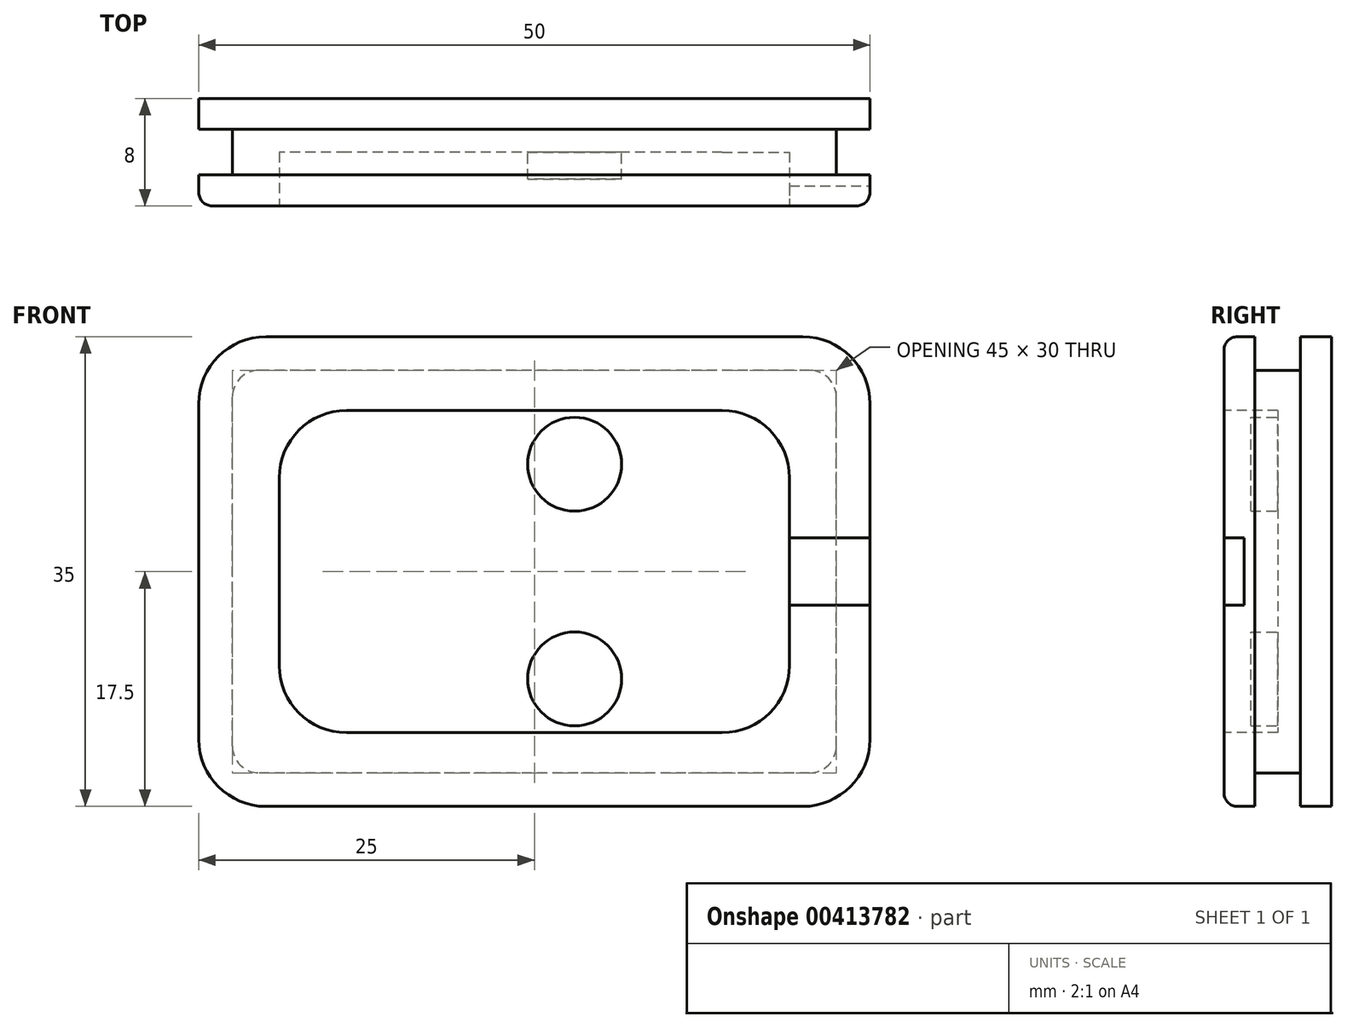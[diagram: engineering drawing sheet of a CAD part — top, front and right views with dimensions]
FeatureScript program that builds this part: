
annotation { "Feature Type Name" : "Feature", "Feature Type Description" : "" }
export const myFeature = defineFeature(function(context is Context, id is Id, definition is map)
    precondition{}
    {
        {
            var Q0;
            Q0=qCreatedBy(makeId("Front.planeOp"),FACE);
            var sketch = newSketch(context, id + "F0", { "sketchPlane" : qUnion([Q0])});
            skLineSegment(sketch, "E0", {"start": v(0, 0) * mm, "end": v(50, 0) * mm});
            skLineSegment(sketch, "E1", {"start": v(50, 0) * mm, "end": v(50, 35) * mm});
            skLineSegment(sketch, "E2", {"start": v(50, 35) * mm, "end": v(0, 35) * mm});
            skLineSegment(sketch, "E3", {"start": v(0, 35) * mm, "end": v(0, 0) * mm});
            skSolve(sketch);
        }
        {
            var Q0;
            Q0=makeQuery(id+"F0.imprint","IMPRINT",FACE,{"disambiguationData":[TD([[makeQuery(id+"F0.imprint","IMPRINT",EDGE,{"derivedFrom":sQuery(id+"F0.wireOp",EDGE,"E0")}),1.0]])]});
            extrude(context, id + "F1", {"entities" : qUnion([Q0]), "depth" : 8 * mm});
        }
        {
            var Q0;
            Q0=makeQuery(id+"F1.opExtrude","CAP_FACE",FACE,{"disambiguationData":[OSD([sQuery(id+"F0.wireOp",EDGE,"E0"),sQuery(id+"F0.wireOp",EDGE,"E1"),sQuery(id+"F0.wireOp",EDGE,"E2"),sQuery(id+"F0.wireOp",EDGE,"E3")])],"isStart":false});
            var sketch = newSketch(context, id + "F2", { "sketchPlane" : qUnion([Q0])});
            skLineSegment(sketch, "E4", {"start": v(6, 5.5) * mm, "end": v(44, 5.5) * mm});
            skLineSegment(sketch, "E5", {"start": v(44, 29.5) * mm, "end": v(6, 29.5) * mm});
            skLineSegment(sketch, "E6", {"start": v(6, 29.5) * mm, "end": v(6, 5.5) * mm});
            skLineSegment(sketch, "E7", {"start": v(44, 29.5) * mm, "end": v(44, 5.5) * mm});
            skSolve(sketch);
        }
        {
            var Q0;
            Q0=makeQuery(id+"F2.imprint","IMPRINT",FACE,{"disambiguationData":[TD([[makeQuery(id+"F2.imprint","IMPRINT",EDGE,{"derivedFrom":sQuery(id+"F2.wireOp",EDGE,"E4")}),1.0]])]});
            extrude(context, id + "F3", {"entities" : qUnion([Q0]), "operationType" : NewBodyOperationType.REMOVE, "oppositeDirection" : true, "depth" : 4 * mm});
        }
        {
            var Q0;
            Q0=makeQuery(id+"F3.boolean.opBoolean","COPY",FACE,{"derivedFrom":makeQuery(id+"F3.opExtrude","CAP_FACE",FACE,{"disambiguationData":[OSD([sQuery(id+"F2.wireOp",EDGE,"E4"),sQuery(id+"F2.wireOp",EDGE,"E5"),sQuery(id+"F2.wireOp",EDGE,"E6"),sQuery(id+"F2.wireOp",EDGE,"E7")])],"isStart":false})});
            var sketch = newSketch(context, id + "F4", { "sketchPlane" : qUnion([Q0])});
            skCircle(sketch, "E8", {"center": v(28, 9.5) * mm, "radius": 3.5 * mm});
            skSolve(sketch);
        }
        {
            var Q0;
            Q0=makeQuery(id+"F4.imprint","IMPRINT",FACE,{"disambiguationData":[TD([[makeQuery(id+"F4.imprint","IMPRINT",EDGE,{"derivedFrom":sQuery(id+"F4.wireOp",EDGE,"E8")}),-1.0]])]});
            var sketch = newSketch(context, id + "F5", { "sketchPlane" : qUnion([Q0])});
            skCircle(sketch, "E9", {"center": v(28, 25.5) * mm, "radius": 3.5 * mm});
            skSolve(sketch);
        }
        {
            var Q0;
            Q0=makeQuery(id+"F4.imprint","IMPRINT",FACE,{"disambiguationData":[TD([[makeQuery(id+"F4.imprint","IMPRINT",EDGE,{"derivedFrom":sQuery(id+"F4.wireOp",EDGE,"E8")}),1.0]])]});
            extrude(context, id + "F6", {"entities" : qUnion([Q0]), "operationType" : NewBodyOperationType.ADD, "depth" : 2 * mm});
        }
        {
            var Q0;
            Q0=makeQuery(id+"F5.imprint","IMPRINT",FACE,{"disambiguationData":[TD([[makeQuery(id+"F5.imprint","IMPRINT",EDGE,{"derivedFrom":sQuery(id+"F5.wireOp",EDGE,"E9")}),1.0]])]});
            extrude(context, id + "F7", {"entities" : qUnion([Q0]), "operationType" : NewBodyOperationType.ADD, "depth" : 2 * mm});
        }
        {
            var Q0;
            Q0=makeQuery(id+"F1.opExtrude","CAP_FACE",FACE,{"disambiguationData":[OSD([sQuery(id+"F0.wireOp",EDGE,"E0"),sQuery(id+"F0.wireOp",EDGE,"E1"),sQuery(id+"F0.wireOp",EDGE,"E2"),sQuery(id+"F0.wireOp",EDGE,"E3")])],"isStart":false});
            var sketch = newSketch(context, id + "F8", { "sketchPlane" : qUnion([Q0])});
            skLineSegment(sketch, "E10", {"start": v(44, 20) * mm, "end": v(50, 20) * mm});
            skLineSegment(sketch, "E11", {"start": v(50, 20) * mm, "end": v(50, 15) * mm});
            skLineSegment(sketch, "E12", {"start": v(50, 15) * mm, "end": v(44, 15) * mm});
            skLineSegment(sketch, "E13", {"start": v(44, 15) * mm, "end": v(44, 20) * mm});
            skSolve(sketch);
        }
        {
            var Q0;
            Q0=makeQuery(id+"F8.imprint","IMPRINT",FACE,{"disambiguationData":[TD([[makeQuery(id+"F8.imprint","IMPRINT",EDGE,{"derivedFrom":sQuery(id+"F8.wireOp",EDGE,"E10")}),-1.0]])]});
            extrude(context, id + "F9", {"entities" : qUnion([Q0]), "operationType" : NewBodyOperationType.REMOVE, "oppositeDirection" : true, "depth" : 1.5 * mm});
        }
        {
            var Q0;
            Q0=makeQuery(id+"F1.opExtrude","SWEPT_FACE",FACE,{"disambiguationData":[OSD([sQuery(id+"F0.wireOp",EDGE,"E0")])]});
            var sketch = newSketch(context, id + "F10", { "sketchPlane" : qUnion([Q0])});
            skLineSegment(sketch, "E14", {"start": v(0, 5.7) * mm, "end": v(50, 5.7) * mm});
            skLineSegment(sketch, "E15", {"start": v(50, 5.7) * mm, "end": v(50, 2.3) * mm});
            skLineSegment(sketch, "E16", {"start": v(50, 2.3) * mm, "end": v(0, 2.3) * mm});
            skLineSegment(sketch, "E17", {"start": v(0, 2.3) * mm, "end": v(0, 5.7) * mm});
            skSolve(sketch);
        }
        {
            var Q0;
            Q0=makeQuery(id+"F1.opExtrude","SWEPT_FACE",FACE,{"disambiguationData":[OSD([sQuery(id+"F0.wireOp",EDGE,"E3")])]});
            var sketch = newSketch(context, id + "F11", { "sketchPlane" : qUnion([Q0])});
            skLineSegment(sketch, "E18", {"start": v(5.7, 35) * mm, "end": v(5.7, 0) * mm});
            skLineSegment(sketch, "E19", {"start": v(5.7, 0) * mm, "end": v(2.3, 0) * mm});
            skLineSegment(sketch, "E20", {"start": v(2.3, 0) * mm, "end": v(2.3, 35) * mm});
            skLineSegment(sketch, "E21", {"start": v(2.3, 35) * mm, "end": v(5.7, 35) * mm});
            skSolve(sketch);
        }
        {
            var Q0;
            Q0=makeQuery(id+"F1.opExtrude","SWEPT_FACE",FACE,{"disambiguationData":[OSD([sQuery(id+"F0.wireOp",EDGE,"E2")])]});
            var sketch = newSketch(context, id + "F12", { "sketchPlane" : qUnion([Q0])});
            skLineSegment(sketch, "E22", {"start": v(50, -5.7) * mm, "end": v(0, -5.7) * mm});
            skLineSegment(sketch, "E23", {"start": v(0, -5.7) * mm, "end": v(0, -2.3) * mm});
            skLineSegment(sketch, "E24", {"start": v(0, -2.3) * mm, "end": v(50, -2.3) * mm});
            skLineSegment(sketch, "E25", {"start": v(50, -2.3) * mm, "end": v(50, -5.7) * mm});
            skSolve(sketch);
        }
        {
            var Q0;
            Q0=makeQuery(id+"F1.opExtrude","SWEPT_FACE",FACE,{"disambiguationData":[OSD([sQuery(id+"F0.wireOp",EDGE,"E1")])]});
            var sketch = newSketch(context, id + "F13", { "sketchPlane" : qUnion([Q0])});
            skLineSegment(sketch, "E26", {"start": v(-5.7, 0) * mm, "end": v(-5.7, 35) * mm});
            skLineSegment(sketch, "E27", {"start": v(-5.7, 35) * mm, "end": v(-2.3, 35) * mm});
            skLineSegment(sketch, "E28", {"start": v(-2.3, 35) * mm, "end": v(-2.3, 0) * mm});
            skLineSegment(sketch, "E29", {"start": v(-2.3, 0) * mm, "end": v(-5.7, 0) * mm});
            skSolve(sketch);
        }
        {
            var Q0;
            Q0=makeQuery(id+"F10.imprint","IMPRINT",FACE,{"disambiguationData":[TD([[makeQuery(id+"F10.imprint","IMPRINT",EDGE,{"derivedFrom":sQuery(id+"F10.wireOp",EDGE,"E14")}),-1.0]])]});
            extrude(context, id + "F14", {"entities" : qUnion([Q0]), "operationType" : NewBodyOperationType.REMOVE, "oppositeDirection" : true, "depth" : 2.5 * mm});
        }
        {
            var Q0;
            Q0=makeQuery(id+"F11.imprint","IMPRINT",FACE,{"disambiguationData":[TD([[makeQuery(id+"F11.imprint","IMPRINT",EDGE,{"derivedFrom":sQuery(id+"F11.wireOp",EDGE,"E18")}),-1.0]])]});
            extrude(context, id + "F15", {"entities" : qUnion([Q0]), "operationType" : NewBodyOperationType.REMOVE, "oppositeDirection" : true, "depth" : 2.5 * mm});
        }
        {
            var Q0;
            Q0=makeQuery(id+"F12.imprint","IMPRINT",FACE,{"disambiguationData":[TD([[makeQuery(id+"F12.imprint","IMPRINT",EDGE,{"derivedFrom":sQuery(id+"F12.wireOp",EDGE,"E22")}),-1.0]])]});
            extrude(context, id + "F16", {"entities" : qUnion([Q0]), "operationType" : NewBodyOperationType.REMOVE, "oppositeDirection" : true, "depth" : 2.5 * mm});
        }
        {
            var Q0;
            Q0=makeQuery(id+"F13.imprint","IMPRINT",FACE,{"disambiguationData":[TD([[makeQuery(id+"F13.imprint","IMPRINT",EDGE,{"derivedFrom":sQuery(id+"F13.wireOp",EDGE,"E26")}),-1.0]])]});
            extrude(context, id + "F17", {"entities" : qUnion([Q0]), "operationType" : NewBodyOperationType.REMOVE, "oppositeDirection" : true, "depth" : 2.5 * mm});
        }
        {
            var Q0;
            {var subQ0=sQuery(id+"F0.wireOp",EDGE,"E3");var subQ1=sQuery(id+"F0.wireOp",EDGE,"E2");Q0=makeQuery(id+"F15.boolean.opBoolean","SPLIT",EDGE,{"disambiguationData":[TD([makeQuery(id+"F14.boolean.opBoolean","COPY",FACE,{"derivedFrom":makeQuery(id+"F14.opExtrude","SWEPT_FACE",FACE,{"disambiguationData":[OSD([sQuery(id+"F10.wireOp",EDGE,"E14")])]})})])],"derivedFrom":makeQuery(id+"F1.opExtrude","SWEPT_EDGE",EDGE,{"disambiguationData":[OSD([subQ1,subQ0])]})});}
            var Q1;
            {var subQ0=sQuery(id+"F0.wireOp",EDGE,"E3");var subQ1=sQuery(id+"F0.wireOp",EDGE,"E2");Q1=makeQuery(id+"F15.boolean.opBoolean","SPLIT",EDGE,{"disambiguationData":[TD([makeQuery(id+"F14.boolean.opBoolean","COPY",FACE,{"derivedFrom":makeQuery(id+"F14.opExtrude","SWEPT_FACE",FACE,{"disambiguationData":[OSD([sQuery(id+"F10.wireOp",EDGE,"E16")])]})})])],"derivedFrom":makeQuery(id+"F1.opExtrude","SWEPT_EDGE",EDGE,{"disambiguationData":[OSD([subQ1,subQ0])]})});}
            var Q2;
            {var subQ0=sQuery(id+"F0.wireOp",EDGE,"E0");var subQ1=sQuery(id+"F0.wireOp",EDGE,"E3");Q2=makeQuery(id+"F14.boolean.opBoolean","SPLIT",EDGE,{"disambiguationData":[TD([makeQuery(id+"F14.opExtrude","SWEPT_FACE",FACE,{"disambiguationData":[OSD([sQuery(id+"F10.wireOp",EDGE,"E14")])]})])],"derivedFrom":makeQuery(id+"F1.opExtrude","SWEPT_EDGE",EDGE,{"disambiguationData":[OSD([subQ0,subQ1])]})});}
            var Q3;
            {var subQ0=sQuery(id+"F0.wireOp",EDGE,"E0");var subQ1=sQuery(id+"F0.wireOp",EDGE,"E3");Q3=makeQuery(id+"F14.boolean.opBoolean","SPLIT",EDGE,{"disambiguationData":[TD([makeQuery(id+"F14.opExtrude","SWEPT_FACE",FACE,{"disambiguationData":[OSD([sQuery(id+"F10.wireOp",EDGE,"E16")])]})])],"derivedFrom":makeQuery(id+"F1.opExtrude","SWEPT_EDGE",EDGE,{"disambiguationData":[OSD([subQ0,subQ1])]})});}
            var Q4;
            {var subQ0=sQuery(id+"F0.wireOp",EDGE,"E0");var subQ1=sQuery(id+"F0.wireOp",EDGE,"E1");Q4=makeQuery(id+"F14.boolean.opBoolean","SPLIT",EDGE,{"disambiguationData":[TD([makeQuery(id+"F14.opExtrude","SWEPT_FACE",FACE,{"disambiguationData":[OSD([sQuery(id+"F10.wireOp",EDGE,"E14")])]})])],"derivedFrom":makeQuery(id+"F1.opExtrude","SWEPT_EDGE",EDGE,{"disambiguationData":[OSD([subQ0,subQ1])]})});}
            var Q5;
            {var subQ0=sQuery(id+"F0.wireOp",EDGE,"E0");var subQ1=sQuery(id+"F0.wireOp",EDGE,"E1");Q5=makeQuery(id+"F14.boolean.opBoolean","SPLIT",EDGE,{"disambiguationData":[TD([makeQuery(id+"F14.opExtrude","SWEPT_FACE",FACE,{"disambiguationData":[OSD([sQuery(id+"F10.wireOp",EDGE,"E16")])]})])],"derivedFrom":makeQuery(id+"F1.opExtrude","SWEPT_EDGE",EDGE,{"disambiguationData":[OSD([subQ0,subQ1])]})});}
            var Q6;
            {var subQ0=sQuery(id+"F0.wireOp",EDGE,"E2");var subQ1=sQuery(id+"F0.wireOp",EDGE,"E1");Q6=makeQuery(id+"F16.boolean.opBoolean","SPLIT",EDGE,{"disambiguationData":[TD([makeQuery(id+"F14.boolean.opBoolean","COPY",FACE,{"derivedFrom":makeQuery(id+"F14.opExtrude","SWEPT_FACE",FACE,{"disambiguationData":[OSD([sQuery(id+"F10.wireOp",EDGE,"E16")])]})})])],"derivedFrom":makeQuery(id+"F1.opExtrude","SWEPT_EDGE",EDGE,{"disambiguationData":[OSD([subQ1,subQ0])]})});}
            var Q7;
            {var subQ0=sQuery(id+"F0.wireOp",EDGE,"E2");var subQ1=sQuery(id+"F0.wireOp",EDGE,"E1");Q7=makeQuery(id+"F16.boolean.opBoolean","SPLIT",EDGE,{"disambiguationData":[TD([makeQuery(id+"F14.boolean.opBoolean","COPY",FACE,{"derivedFrom":makeQuery(id+"F14.opExtrude","SWEPT_FACE",FACE,{"disambiguationData":[OSD([sQuery(id+"F10.wireOp",EDGE,"E14")])]})})])],"derivedFrom":makeQuery(id+"F1.opExtrude","SWEPT_EDGE",EDGE,{"disambiguationData":[OSD([subQ1,subQ0])]})});}
            var Q8;
            Q8=makeQuery(id+"F3.boolean.opBoolean","COPY",EDGE,{"derivedFrom":makeQuery(id+"F3.opExtrude","SWEPT_EDGE",EDGE,{"disambiguationData":[OSD([sQuery(id+"F2.wireOp",EDGE,"E5"),sQuery(id+"F2.wireOp",EDGE,"E7")])]})});
            var Q9;
            Q9=makeQuery(id+"F3.boolean.opBoolean","COPY",EDGE,{"derivedFrom":makeQuery(id+"F3.opExtrude","SWEPT_EDGE",EDGE,{"disambiguationData":[OSD([sQuery(id+"F2.wireOp",EDGE,"E4"),sQuery(id+"F2.wireOp",EDGE,"E7")])]})});
            var Q10;
            Q10=makeQuery(id+"F3.boolean.opBoolean","COPY",EDGE,{"derivedFrom":makeQuery(id+"F3.opExtrude","SWEPT_EDGE",EDGE,{"disambiguationData":[OSD([sQuery(id+"F2.wireOp",EDGE,"E4"),sQuery(id+"F2.wireOp",EDGE,"E6")])]})});
            var Q11;
            Q11=makeQuery(id+"F3.boolean.opBoolean","COPY",EDGE,{"derivedFrom":makeQuery(id+"F3.opExtrude","SWEPT_EDGE",EDGE,{"disambiguationData":[OSD([sQuery(id+"F2.wireOp",EDGE,"E5"),sQuery(id+"F2.wireOp",EDGE,"E6")])]})});
            fillet(context, id + "F18", {"entities" : qUnion([Q0, Q1, Q2, Q3, Q4, Q5, Q6, Q7, Q8, Q9, Q10, Q11]), "radius" : 5 * mm, "tangentPropagation" : true, "allowEdgeOverflow" : false});
        }
        {
            var Q0;
            Q0=makeQuery(id+"F1.opExtrude","CAP_EDGE",EDGE,{"disambiguationData":[OSD([sQuery(id+"F0.wireOp",EDGE,"E0")])],"isStart":false});
            fillet(context, id + "F19", {"entities" : qUnion([Q0]), "radius" : 1 * mm, "tangentPropagation" : true, "allowEdgeOverflow" : false});
        }
        {
            var Q0;
            Q0=makeQuery(id+"F16.boolean.opBoolean","INTERSECT",EDGE,{"derivedFrom":[makeQuery(id+"F15.boolean.opBoolean","COPY",FACE,{"derivedFrom":makeQuery(id+"F15.opExtrude","CAP_FACE",FACE,{"disambiguationData":[OSD([sQuery(id+"F11.wireOp",EDGE,"E18"),sQuery(id+"F11.wireOp",EDGE,"E19"),sQuery(id+"F11.wireOp",EDGE,"E20"),sQuery(id+"F11.wireOp",EDGE,"E21")])],"isStart":false})}),makeQuery(id+"F16.opExtrude","CAP_FACE",FACE,{"disambiguationData":[OSD([sQuery(id+"F12.wireOp",EDGE,"E22"),sQuery(id+"F12.wireOp",EDGE,"E23"),sQuery(id+"F12.wireOp",EDGE,"E24"),sQuery(id+"F12.wireOp",EDGE,"E25")])],"isStart":false})]});
            var Q1;
            Q1=makeQuery(id+"F15.boolean.opBoolean","INTERSECT",EDGE,{"derivedFrom":[makeQuery(id+"F14.boolean.opBoolean","COPY",FACE,{"derivedFrom":makeQuery(id+"F14.opExtrude","CAP_FACE",FACE,{"disambiguationData":[OSD([sQuery(id+"F10.wireOp",EDGE,"E14"),sQuery(id+"F10.wireOp",EDGE,"E15"),sQuery(id+"F10.wireOp",EDGE,"E16"),sQuery(id+"F10.wireOp",EDGE,"E17")])],"isStart":false})}),makeQuery(id+"F15.opExtrude","CAP_FACE",FACE,{"disambiguationData":[OSD([sQuery(id+"F11.wireOp",EDGE,"E18"),sQuery(id+"F11.wireOp",EDGE,"E19"),sQuery(id+"F11.wireOp",EDGE,"E20"),sQuery(id+"F11.wireOp",EDGE,"E21")])],"isStart":false})]});
            var Q2;
            Q2=makeQuery(id+"F17.boolean.opBoolean","INTERSECT",EDGE,{"derivedFrom":[makeQuery(id+"F14.boolean.opBoolean","COPY",FACE,{"derivedFrom":makeQuery(id+"F14.opExtrude","CAP_FACE",FACE,{"disambiguationData":[OSD([sQuery(id+"F10.wireOp",EDGE,"E14"),sQuery(id+"F10.wireOp",EDGE,"E15"),sQuery(id+"F10.wireOp",EDGE,"E16"),sQuery(id+"F10.wireOp",EDGE,"E17")])],"isStart":false})}),makeQuery(id+"F17.opExtrude","CAP_FACE",FACE,{"disambiguationData":[OSD([sQuery(id+"F13.wireOp",EDGE,"E26"),sQuery(id+"F13.wireOp",EDGE,"E27"),sQuery(id+"F13.wireOp",EDGE,"E28"),sQuery(id+"F13.wireOp",EDGE,"E29")])],"isStart":false})]});
            var Q3;
            Q3=makeQuery(id+"F17.boolean.opBoolean","INTERSECT",EDGE,{"derivedFrom":[makeQuery(id+"F16.boolean.opBoolean","COPY",FACE,{"derivedFrom":makeQuery(id+"F16.opExtrude","CAP_FACE",FACE,{"disambiguationData":[OSD([sQuery(id+"F12.wireOp",EDGE,"E22"),sQuery(id+"F12.wireOp",EDGE,"E23"),sQuery(id+"F12.wireOp",EDGE,"E24"),sQuery(id+"F12.wireOp",EDGE,"E25")])],"isStart":false})}),makeQuery(id+"F17.opExtrude","CAP_FACE",FACE,{"disambiguationData":[OSD([sQuery(id+"F13.wireOp",EDGE,"E26"),sQuery(id+"F13.wireOp",EDGE,"E27"),sQuery(id+"F13.wireOp",EDGE,"E28"),sQuery(id+"F13.wireOp",EDGE,"E29")])],"isStart":false})]});
            fillet(context, id + "F20", {"entities" : qUnion([Q0, Q1, Q2, Q3]), "radius" : 2 * mm, "tangentPropagation" : true, "allowEdgeOverflow" : false});
        }
    });
